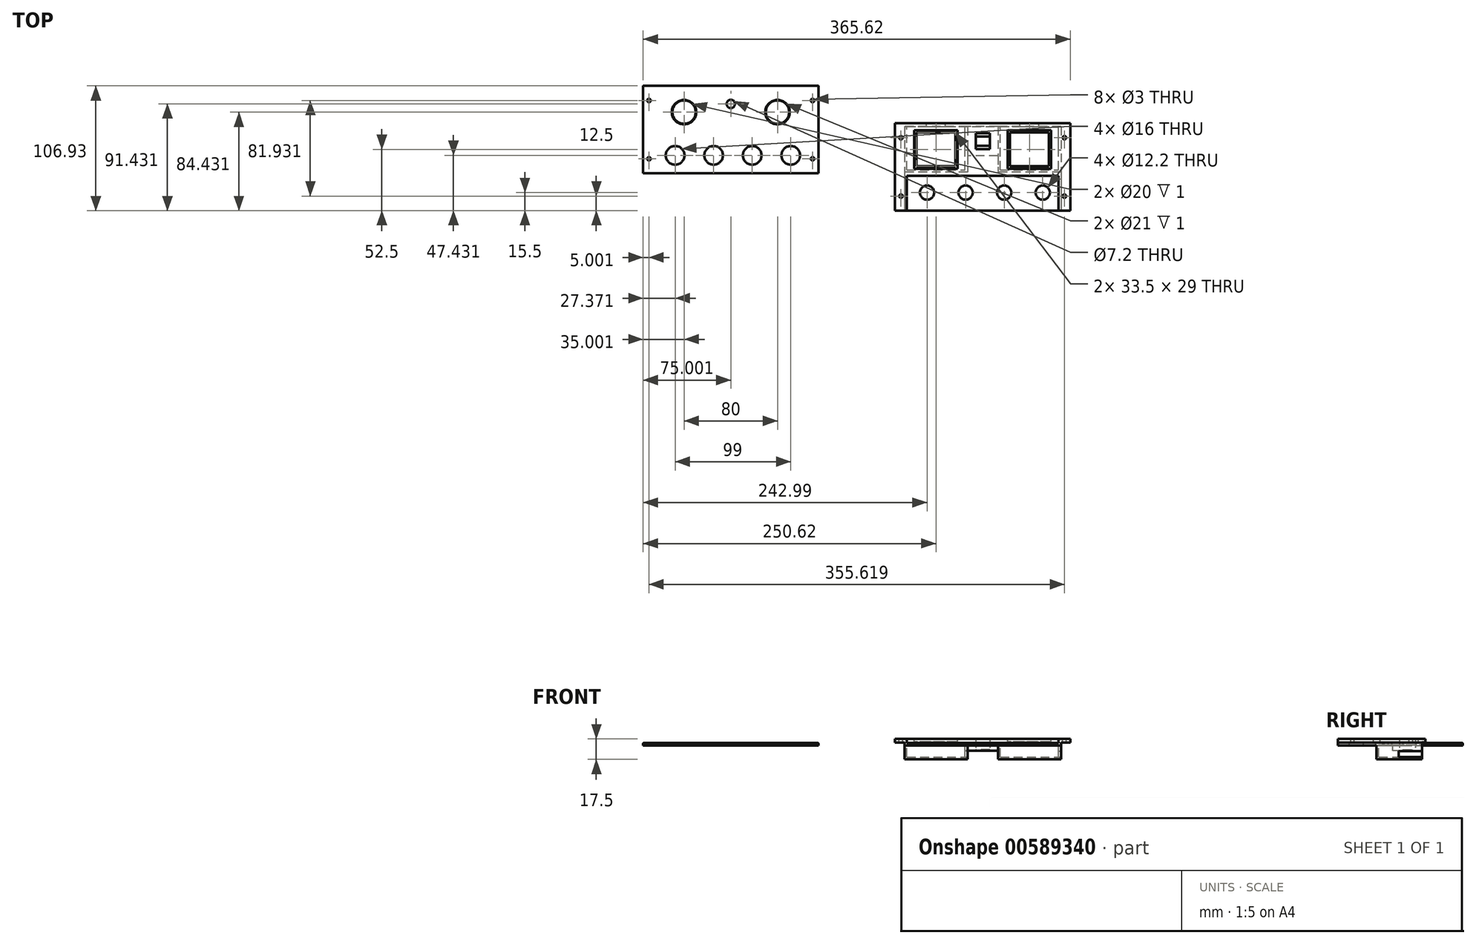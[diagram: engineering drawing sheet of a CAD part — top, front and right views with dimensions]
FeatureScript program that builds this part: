
annotation { "Feature Type Name" : "Feature", "Feature Type Description" : "" }
export const myFeature = defineFeature(function(context is Context, id is Id, definition is map)
    precondition{}
    {
        {
            var Q0;
            Q0=qCreatedBy(makeId("Top.planeOp"),FACE);
            var sketch = newSketch(context, id + "F0", { "sketchPlane" : qUnion([Q0])});
            skLineSegment(sketch, "E0.bottom", {"start": v(75, -37.5) * mm, "end": v(-75, -37.5) * mm});
            skLineSegment(sketch, "E0.top", {"start": v(75, 37.5) * mm, "end": v(-75, 37.5) * mm});
            skLineSegment(sketch, "E0.left", {"start": v(75, -37.5) * mm, "end": v(75, 37.5) * mm});
            skLineSegment(sketch, "E0.right", {"start": v(-75, -37.5) * mm, "end": v(-75, 37.5) * mm});
            skPoint(sketch, "E0.middle", {"position": v(0, 0) * mm});
            skCircle(sketch, "E1", {"center": v(0, 22) * mm, "radius": 5 * mm, "construction": true});
            skCircle(sketch, "E2", {"center": v(-47.63, -22) * mm, "radius": 6.1 * mm});
            skCircle(sketch, "E3.1.0.0", {"center": v(-14.63, -22) * mm, "radius": 6.1 * mm});
            skCircle(sketch, "E3.2.0.0", {"center": v(18.37, -22) * mm, "radius": 6.1 * mm});
            skCircle(sketch, "E3.3.0.0", {"center": v(51.37, -22) * mm, "radius": 6.1 * mm});
            skLineSegment(sketch, "E3.direction1", {"start": v(-47.63, -22) * mm, "end": v(-14.63, -22) * mm, "construction": true});
            skLineSegment(sketch, "E4.bottom", {"start": v(-75, 37.5) * mm, "end": v(-65, 37.5) * mm, "construction": true});
            skLineSegment(sketch, "E4.top", {"start": v(-75, -37.5) * mm, "end": v(-65, -37.5) * mm, "construction": true});
            skLineSegment(sketch, "E4.left", {"start": v(-75, 37.5) * mm, "end": v(-75, -37.5) * mm, "construction": true});
            skLineSegment(sketch, "E4.right", {"start": v(-65, 37.5) * mm, "end": v(-65, -37.5) * mm, "construction": true});
            skLineSegment(sketch, "E5.bottom", {"start": v(75, 37.5) * mm, "end": v(65, 37.5) * mm, "construction": true});
            skLineSegment(sketch, "E5.top", {"start": v(75, -37.5) * mm, "end": v(65, -37.5) * mm, "construction": true});
            skLineSegment(sketch, "E5.left", {"start": v(75, 37.5) * mm, "end": v(75, -37.5) * mm, "construction": true});
            skLineSegment(sketch, "E5.right", {"start": v(65, 37.5) * mm, "end": v(65, -37.5) * mm, "construction": true});
            skPoint(sketch, "E6.middle", {"position": v(-40, 15) * mm});
            skLineSegment(sketch, "E7.bottom", {"start": v(-23.25, 0.5) * mm, "end": v(-56.75, 0.5) * mm});
            skLineSegment(sketch, "E7.top", {"start": v(-23.25, 29.5) * mm, "end": v(-56.75, 29.5) * mm});
            skLineSegment(sketch, "E7.left", {"start": v(-23.25, 0.5) * mm, "end": v(-23.25, 29.5) * mm});
            skLineSegment(sketch, "E7.right", {"start": v(-56.75, 0.5) * mm, "end": v(-56.75, 29.5) * mm});
            skLineSegment(sketch, "E8.bottom", {"start": v(56.75, 0.5) * mm, "end": v(23.25, 0.5) * mm});
            skLineSegment(sketch, "E8.top", {"start": v(56.75, 29.5) * mm, "end": v(23.25, 29.5) * mm});
            skLineSegment(sketch, "E8.left", {"start": v(56.75, 0.5) * mm, "end": v(56.75, 29.5) * mm});
            skLineSegment(sketch, "E8.right", {"start": v(23.25, 0.5) * mm, "end": v(23.25, 29.5) * mm});
            skPoint(sketch, "E8.middle", {"position": v(40, 15) * mm});
            skPoint(sketch, "E9.centerSnap0", {"position": v(-70, 37.5) * mm});
            skCircle(sketch, "E10", {"center": v(-70, 25) * mm, "radius": 1.5 * mm});
            skCircle(sketch, "E11", {"center": v(-70, -25) * mm, "radius": 1.5 * mm});
            skCircle(sketch, "E12", {"center": v(70, 25) * mm, "radius": 1.5 * mm});
            skCircle(sketch, "E13", {"center": v(70, -25) * mm, "radius": 1.5 * mm});
            skLineSegment(sketch, "E14.bottom", {"start": v(6, 15.25) * mm, "end": v(-6, 15.25) * mm});
            skLineSegment(sketch, "E14.top", {"start": v(6, 28.75) * mm, "end": v(-6, 28.75) * mm});
            skLineSegment(sketch, "E14.left", {"start": v(6, 15.25) * mm, "end": v(6, 28.75) * mm});
            skLineSegment(sketch, "E14.right", {"start": v(-6, 15.25) * mm, "end": v(-6, 28.75) * mm});
            skLineSegment(sketch, "E15.bottom", {"start": v(6, 18) * mm, "end": v(-6, 18) * mm});
            skLineSegment(sketch, "E15.top", {"start": v(6, 26) * mm, "end": v(-6, 26) * mm});
            skLineSegment(sketch, "E15.left", {"start": v(6, 18) * mm, "end": v(6, 26) * mm});
            skLineSegment(sketch, "E15.right", {"start": v(-6, 18) * mm, "end": v(-6, 26) * mm});
            skSolve(sketch);
        }
        {
            var Q0;
            Q0=makeQuery(id+"F0.imprint","IMPRINT",FACE,{"disambiguationData":[TD([[makeQuery(id+"F0.imprint","IMPRINT",EDGE,{"derivedFrom":sQuery(id+"F0.wireOp",EDGE,"E0.bottom")}),-1.0]])]});
            var Q1;
            Q1=makeQuery(id+"F0.imprint","IMPRINT",FACE,{"disambiguationData":[TD([[makeQuery(id+"F0.imprint","IMPRINT",EDGE,{"derivedFrom":sQuery(id+"F0.wireOp",EDGE,"drD5jItb-HEpr-sxaA-TqkW-DfUxLCmm6Exs")}),-1.0]])]});
            var Q2;
            Q2=makeQuery(id+"F0.imprint","IMPRINT",FACE,{"disambiguationData":[TD([[makeQuery(id+"F0.imprint","IMPRINT",EDGE,{"derivedFrom":sQuery(id+"F0.wireOp",EDGE,"E15.bottom")}),-1.0]])]});
            extrude(context, id + "F1", {"entities" : qUnion([Q0, Q1, Q2]), "depth" : 2 * mm});
        }
        {
            var Q0;
            Q0=makeQuery(id+"F1.opExtrude","CAP_FACE",FACE,{"disambiguationData":[OSD([sQuery(id+"F0.wireOp",EDGE,"E0.bottom"),sQuery(id+"F0.wireOp",EDGE,"E0.top"),sQuery(id+"F0.wireOp",EDGE,"E0.left"),sQuery(id+"F0.wireOp",EDGE,"E0.right"),sQuery(id+"F0.wireOp",EDGE,"drD5jItb-HEpr-sxaA-TqkW-DfUxLCmm6Exs"),sQuery(id+"F0.wireOp",EDGE,"oSn99fef-1uPw-k3Do-L9e6-x1k65rtnndGm"),sQuery(id+"F0.wireOp",EDGE,"E1"),sQuery(id+"F0.wireOp",EDGE,"E2"),sQuery(id+"F0.wireOp",EDGE,"E3.1.0.0"),sQuery(id+"F0.wireOp",EDGE,"E3.2.0.0"),sQuery(id+"F0.wireOp",EDGE,"E3.3.0.0")])],"isStart":false});
            var sketch = newSketch(context, id + "F2", { "sketchPlane" : qUnion([Q0])});
            skLineSegment(sketch, "E16.bottom", {"start": v(-75, 37.5) * mm, "end": v(-65, 37.5) * mm});
            skLineSegment(sketch, "E16.top", {"start": v(-75, -37.5) * mm, "end": v(-65, -37.5) * mm});
            skLineSegment(sketch, "E16.left", {"start": v(-75, 37.5) * mm, "end": v(-75, -37.5) * mm});
            skLineSegment(sketch, "E16.right", {"start": v(-65, 37.5) * mm, "end": v(-65, -37.5) * mm});
            skLineSegment(sketch, "E17.bottom", {"start": v(75, -37.5) * mm, "end": v(65, -37.5) * mm});
            skLineSegment(sketch, "E17.top", {"start": v(75, 37.5) * mm, "end": v(65, 37.5) * mm});
            skLineSegment(sketch, "E17.left", {"start": v(75, -37.5) * mm, "end": v(75, 37.5) * mm});
            skLineSegment(sketch, "E17.right", {"start": v(65, -37.5) * mm, "end": v(65, 37.5) * mm});
            skSolve(sketch);
        }
        {
            var Q0;
            Q0=qSketchRegion(id+"F2",true);
            extrude(context, id + "F3", {"entities" : qUnion([Q0]), "operationType" : NewBodyOperationType.ADD, "depth" : 3.5 * mm});
        }
        {
            var Q0;
            Q0=makeQuery(id+"F3.boolean.opBoolean","MERGE",FACE,{"derivedFrom":[makeQuery(id+"F1.opExtrude","SWEPT_FACE",FACE,{"disambiguationData":[OSD([sQuery(id+"F0.wireOp",EDGE,"E0.bottom")])]}),makeQuery(id+"F3.opExtrude","SWEPT_FACE",FACE,{"disambiguationData":[OSD([sQuery(id+"F2.wireOp",EDGE,"E16.top")])]}),makeQuery(id+"F3.opExtrude","SWEPT_FACE",FACE,{"disambiguationData":[OSD([sQuery(id+"F2.wireOp",EDGE,"E17.bottom")])]})]});
            var sketch = newSketch(context, id + "F4", { "sketchPlane" : qUnion([Q0])});
            skLineSegment(sketch, "E18.bottom", {"start": v(-75, 0) * mm, "end": v(-67, 0) * mm});
            skLineSegment(sketch, "E18.top", {"start": v(-75, 2.5) * mm, "end": v(-67, 2.5) * mm});
            skLineSegment(sketch, "E18.left", {"start": v(-75, 0) * mm, "end": v(-75, 2.5) * mm});
            skLineSegment(sketch, "E18.right", {"start": v(-67, 0) * mm, "end": v(-67, 2.5) * mm});
            skLineSegment(sketch, "E19.bottom", {"start": v(75, 0) * mm, "end": v(67, 0) * mm});
            skLineSegment(sketch, "E19.top", {"start": v(75, 2.5) * mm, "end": v(67, 2.5) * mm});
            skLineSegment(sketch, "E19.left", {"start": v(75, 0) * mm, "end": v(75, 2.5) * mm});
            skLineSegment(sketch, "E19.right", {"start": v(67, 0) * mm, "end": v(67, 2.5) * mm});
            skSolve(sketch);
        }
        {
            var Q0;
            Q0=qSketchRegion(id+"F4",true);
            extrude(context, id + "F5", {"entities" : qUnion([Q0]), "operationType" : NewBodyOperationType.REMOVE, "oppositeDirection" : true, "depth" : 80 * mm});
        }
        {
            var Q0;
            Q0=makeQuery(id+"F1.opExtrude","CAP_FACE",FACE,{"disambiguationData":[OSD([sQuery(id+"F0.wireOp",EDGE,"E0.bottom"),sQuery(id+"F0.wireOp",EDGE,"E0.top"),sQuery(id+"F0.wireOp",EDGE,"E0.left"),sQuery(id+"F0.wireOp",EDGE,"E0.right"),sQuery(id+"F0.wireOp",EDGE,"drD5jItb-HEpr-sxaA-TqkW-DfUxLCmm6Exs"),sQuery(id+"F0.wireOp",EDGE,"oSn99fef-1uPw-k3Do-L9e6-x1k65rtnndGm"),sQuery(id+"F0.wireOp",EDGE,"E1"),sQuery(id+"F0.wireOp",EDGE,"E2"),sQuery(id+"F0.wireOp",EDGE,"E3.1.0.0"),sQuery(id+"F0.wireOp",EDGE,"E3.2.0.0"),sQuery(id+"F0.wireOp",EDGE,"E3.3.0.0")])],"isStart":false});
            var sketch = newSketch(context, id + "F6", { "sketchPlane" : qUnion([Q0])});
            skLineSegment(sketch, "E20.bottom", {"start": v(-65, 37.5) * mm, "end": v(65, 37.5) * mm});
            skLineSegment(sketch, "E20.top", {"start": v(-65, -7.5) * mm, "end": v(65, -7.5) * mm});
            skLineSegment(sketch, "E20.left", {"start": v(-65, 37.5) * mm, "end": v(-65, -7.5) * mm});
            skLineSegment(sketch, "E20.right", {"start": v(65, 37.5) * mm, "end": v(65, -7.5) * mm});
            skCircle(sketch, "E21", {"center": v(0, 22) * mm, "radius": 5 * mm, "construction": true});
            skLineSegment(sketch, "E22.bottom", {"start": v(-23.25, 0.5) * mm, "end": v(-56.75, 0.5) * mm});
            skLineSegment(sketch, "E22.top", {"start": v(-23.25, 29.5) * mm, "end": v(-56.75, 29.5) * mm});
            skLineSegment(sketch, "E22.left", {"start": v(-23.25, 0.5) * mm, "end": v(-23.25, 29.5) * mm});
            skLineSegment(sketch, "E22.right", {"start": v(-56.75, 0.5) * mm, "end": v(-56.75, 29.5) * mm});
            skPoint(sketch, "E22.middle", {"position": v(-40, 15) * mm});
            skLineSegment(sketch, "E23.bottom", {"start": v(56.75, 0.5) * mm, "end": v(23.25, 0.5) * mm});
            skLineSegment(sketch, "E23.top", {"start": v(56.75, 29.5) * mm, "end": v(23.25, 29.5) * mm});
            skLineSegment(sketch, "E23.left", {"start": v(56.75, 0.5) * mm, "end": v(56.75, 29.5) * mm});
            skLineSegment(sketch, "E23.right", {"start": v(23.25, 0.5) * mm, "end": v(23.25, 29.5) * mm});
            skPoint(sketch, "E23.middle", {"position": v(40, 15) * mm});
            skLineSegment(sketch, "E24.bottom", {"start": v(6, 15.25) * mm, "end": v(-6, 15.25) * mm});
            skLineSegment(sketch, "E24.top", {"start": v(6, 28.75) * mm, "end": v(-6, 28.75) * mm});
            skLineSegment(sketch, "E24.left", {"start": v(6, 15.25) * mm, "end": v(6, 28.75) * mm});
            skLineSegment(sketch, "E24.right", {"start": v(-6, 15.25) * mm, "end": v(-6, 28.75) * mm});
            skSolve(sketch);
        }
        {
            var Q0;
            Q0=qSketchRegion(id+"F6",true);
            extrude(context, id + "F7", {"entities" : qUnion([Q0]), "operationType" : NewBodyOperationType.ADD, "depth" : 3.5 * mm});
        }
        {
            var Q0;
            Q0=makeQuery(id+"F7.boolean.opBoolean","MERGE",FACE,{"derivedFrom":[makeQuery(id+"F3.opExtrude","CAP_FACE",FACE,{"disambiguationData":[OSD([sQuery(id+"F2.wireOp",EDGE,"E16.bottom"),sQuery(id+"F2.wireOp",EDGE,"E16.top"),sQuery(id+"F2.wireOp",EDGE,"E16.left"),sQuery(id+"F2.wireOp",EDGE,"E16.right")])],"isStart":false}),makeQuery(id+"F3.opExtrude","CAP_FACE",FACE,{"disambiguationData":[OSD([sQuery(id+"F2.wireOp",EDGE,"E17.bottom"),sQuery(id+"F2.wireOp",EDGE,"E17.top"),sQuery(id+"F2.wireOp",EDGE,"E17.left"),sQuery(id+"F2.wireOp",EDGE,"E17.right")])],"isStart":false}),makeQuery(id+"F7.opExtrude","CAP_FACE",FACE,{"disambiguationData":[OSD([sQuery(id+"F6.wireOp",EDGE,"E20.bottom"),sQuery(id+"F6.wireOp",EDGE,"E20.top"),sQuery(id+"F6.wireOp",EDGE,"E20.left"),sQuery(id+"F6.wireOp",EDGE,"E20.right"),sQuery(id+"F6.wireOp",EDGE,"H2Zb9yD0-p2Z7-Kh5e-a6hj-aLUdcpXocAIw"),sQuery(id+"F6.wireOp",EDGE,"7ZJ2aJG6-LJXW-fwXF-v4kC-qdLRGwjfnqPK"),sQuery(id+"F6.wireOp",EDGE,"E21")])],"isStart":false})]});
            var sketch = newSketch(context, id + "F8", { "sketchPlane" : qUnion([Q0])});
            skLineSegment(sketch, "E25.bottom", {"start": v(-21.4, -1.5) * mm, "end": v(-58.6, -1.5) * mm});
            skLineSegment(sketch, "E25.top", {"start": v(-21.4, 31.5) * mm, "end": v(-58.6, 31.5) * mm});
            skLineSegment(sketch, "E25.left", {"start": v(-21.4, -1.5) * mm, "end": v(-21.4, 31.5) * mm});
            skLineSegment(sketch, "E25.right", {"start": v(-58.6, -1.5) * mm, "end": v(-58.6, 31.5) * mm});
            skPoint(sketch, "E25.middle", {"position": v(-40, 15) * mm});
            skLineSegment(sketch, "E26.bottom", {"start": v(58.6, -1.5) * mm, "end": v(21.4, -1.5) * mm});
            skLineSegment(sketch, "E26.top", {"start": v(58.6, 31.5) * mm, "end": v(21.4, 31.5) * mm});
            skLineSegment(sketch, "E26.left", {"start": v(58.6, -1.5) * mm, "end": v(58.6, 31.5) * mm});
            skLineSegment(sketch, "E26.right", {"start": v(21.4, -1.5) * mm, "end": v(21.4, 31.5) * mm});
            skPoint(sketch, "E26.middle", {"position": v(40, 15) * mm});
            skLineSegment(sketch, "E27.bottom", {"start": v(-32, 31.5) * mm, "end": v(-48, 31.5) * mm});
            skLineSegment(sketch, "E27.top", {"start": v(-32, 46.5) * mm, "end": v(-48, 46.5) * mm});
            skLineSegment(sketch, "E27.left", {"start": v(-32, 31.5) * mm, "end": v(-32, 46.5) * mm});
            skLineSegment(sketch, "E27.right", {"start": v(-48, 31.5) * mm, "end": v(-48, 46.5) * mm});
            skPoint(sketch, "E27.middle", {"position": v(-40, 39) * mm});
            skPoint(sketch, "E27.middle.positionSnap0", {"position": v(-40, 31.5) * mm});
            skPoint(sketch, "E27.centerSnap0", {"position": v(-40, 31.5) * mm});
            skLineSegment(sketch, "E28.bottom", {"start": v(48, 31.5) * mm, "end": v(32, 31.5) * mm});
            skLineSegment(sketch, "E28.top", {"start": v(48, 46.5) * mm, "end": v(32, 46.5) * mm});
            skLineSegment(sketch, "E28.left", {"start": v(48, 31.5) * mm, "end": v(48, 46.5) * mm});
            skLineSegment(sketch, "E28.right", {"start": v(32, 31.5) * mm, "end": v(32, 46.5) * mm});
            skPoint(sketch, "E28.middle", {"position": v(40, 39) * mm});
            skPoint(sketch, "E28.middle.positionSnap0", {"position": v(40, 31.5) * mm});
            skPoint(sketch, "E28.centerSnap0", {"position": v(40, 31.5) * mm});
            skSolve(sketch);
        }
        {
            var Q0;
            Q0=makeQuery(id+"F8.imprint","IMPRINT",FACE,{"disambiguationData":[TD([[makeQuery(id+"F8.imprint","IMPRINT",EDGE,{"derivedFrom":sQuery(id+"F8.wireOp",EDGE,"E25.bottom")}),-1.0]])]});
            var Q1;
            Q1=makeQuery(id+"F8.imprint","IMPRINT",FACE,{"disambiguationData":[TD([[makeQuery(id+"F8.imprint","IMPRINT",EDGE,{"derivedFrom":sQuery(id+"F8.wireOp",EDGE,"E26.bottom")}),-1.0]])]});
            var Q2;
            {var subQ0=sQuery(id+"F8.wireOp",EDGE,"E27.top");Q2=makeQuery(id+"F8.imprint","IMPRINT",FACE,{"disambiguationData":[TD([[makeQuery(id+"F8.imprint","IMPRINT",EDGE,{"derivedFrom":subQ0}),1.0]])]});}
            var Q3;
            {var subQ0=sQuery(id+"F8.wireOp",EDGE,"E28.top");Q3=makeQuery(id+"F8.imprint","IMPRINT",FACE,{"disambiguationData":[TD([[makeQuery(id+"F8.imprint","IMPRINT",EDGE,{"derivedFrom":subQ0}),1.0]])]});}
            var Q4;
            {var subQ0=sQuery(id+"F8.wireOp",EDGE,"E27.bottom");Q4=makeQuery(id+"F8.imprint","IMPRINT",FACE,{"disambiguationData":[TD([[makeQuery(id+"F8.imprint","IMPRINT",EDGE,{"derivedFrom":subQ0}),-1.0]])]});}
            var Q5;
            {var subQ0=sQuery(id+"F8.wireOp",EDGE,"E28.bottom");Q5=makeQuery(id+"F8.imprint","IMPRINT",FACE,{"disambiguationData":[TD([[makeQuery(id+"F8.imprint","IMPRINT",EDGE,{"derivedFrom":subQ0}),-1.0]])]});}
            extrude(context, id + "F9", {"entities" : qUnion([Q0, Q1, Q2, Q3, Q4, Q5]), "operationType" : NewBodyOperationType.REMOVE, "oppositeDirection" : true, "depth" : 2.5 * mm});
        }
        {
            var Q0;
            Q0=qCreatedBy(makeId("Top.planeOp"),FACE);
            var sketch = newSketch(context, id + "F10", { "sketchPlane" : qUnion([Q0])});
            skLineSegment(sketch, "E29.bottom", {"start": v(-140.62, -5.57) * mm, "end": v(-290.62, -5.57) * mm});
            skLineSegment(sketch, "E29.top", {"start": v(-140.62, 69.43) * mm, "end": v(-290.62, 69.43) * mm});
            skLineSegment(sketch, "E29.left", {"start": v(-140.62, -5.57) * mm, "end": v(-140.62, 69.43) * mm});
            skLineSegment(sketch, "E29.right", {"start": v(-290.62, -5.57) * mm, "end": v(-290.62, 69.43) * mm});
            skPoint(sketch, "E29.middle", {"position": v(-215.62, 31.93) * mm});
            skCircle(sketch, "E30", {"center": v(-215.62, 53.93) * mm, "radius": 3.6 * mm});
            skCircle(sketch, "E31", {"center": v(-263.25, 9.93) * mm, "radius": 8 * mm});
            skCircle(sketch, "E32.1.0.0", {"center": v(-230.25, 9.93) * mm, "radius": 8 * mm});
            skCircle(sketch, "E32.2.0.0", {"center": v(-197.25, 9.93) * mm, "radius": 8 * mm});
            skCircle(sketch, "E32.3.0.0", {"center": v(-164.25, 9.93) * mm, "radius": 8 * mm});
            skLineSegment(sketch, "E32.direction1", {"start": v(-263.25, 9.93) * mm, "end": v(-230.25, 9.93) * mm, "construction": true});
            skLineSegment(sketch, "E33.bottom", {"start": v(-290.62, 69.43) * mm, "end": v(-280.62, 69.43) * mm, "construction": true});
            skLineSegment(sketch, "E33.top", {"start": v(-290.62, -5.57) * mm, "end": v(-280.62, -5.57) * mm, "construction": true});
            skLineSegment(sketch, "E33.left", {"start": v(-290.62, 69.43) * mm, "end": v(-290.62, -5.57) * mm, "construction": true});
            skLineSegment(sketch, "E33.right", {"start": v(-280.62, 69.43) * mm, "end": v(-280.62, -5.57) * mm, "construction": true});
            skLineSegment(sketch, "E34.bottom", {"start": v(-140.62, 69.43) * mm, "end": v(-150.62, 69.43) * mm, "construction": true});
            skLineSegment(sketch, "E34.top", {"start": v(-140.62, -5.57) * mm, "end": v(-150.62, -5.57) * mm, "construction": true});
            skLineSegment(sketch, "E34.left", {"start": v(-140.62, 69.43) * mm, "end": v(-140.62, -5.57) * mm, "construction": true});
            skLineSegment(sketch, "E34.right", {"start": v(-150.62, 69.43) * mm, "end": v(-150.62, -5.57) * mm, "construction": true});
            skPoint(sketch, "E35.middle", {"position": v(-255.62, 46.93) * mm});
            skPoint(sketch, "E36.middle", {"position": v(-175.62, 46.93) * mm});
            skCircle(sketch, "E37", {"center": v(-255.62, 46.93) * mm, "radius": 10 * mm});
            skCircle(sketch, "E38", {"center": v(-175.62, 46.93) * mm, "radius": 10 * mm});
            skLineSegment(sketch, "E39.bottom", {"start": v(-236.87, 30.43) * mm, "end": v(-274.37, 30.43) * mm, "construction": true});
            skLineSegment(sketch, "E39.top", {"start": v(-236.87, 63.43) * mm, "end": v(-274.37, 63.43) * mm, "construction": true});
            skLineSegment(sketch, "E39.left", {"start": v(-236.87, 30.43) * mm, "end": v(-236.87, 63.43) * mm, "construction": true});
            skLineSegment(sketch, "E39.right", {"start": v(-274.37, 30.43) * mm, "end": v(-274.37, 63.43) * mm, "construction": true});
            skLineSegment(sketch, "E40.bottom", {"start": v(-156.87, 30.43) * mm, "end": v(-194.37, 30.43) * mm, "construction": true});
            skLineSegment(sketch, "E40.top", {"start": v(-156.87, 63.43) * mm, "end": v(-194.37, 63.43) * mm, "construction": true});
            skLineSegment(sketch, "E40.left", {"start": v(-156.87, 30.43) * mm, "end": v(-156.87, 63.43) * mm, "construction": true});
            skLineSegment(sketch, "E40.right", {"start": v(-194.37, 30.43) * mm, "end": v(-194.37, 63.43) * mm, "construction": true});
            skCircle(sketch, "E41", {"center": v(-285.62, 56.93) * mm, "radius": 1.5 * mm});
            skCircle(sketch, "E42", {"center": v(-285.62, 6.93) * mm, "radius": 1.5 * mm});
            skCircle(sketch, "E43", {"center": v(-145.62, 56.93) * mm, "radius": 1.5 * mm});
            skCircle(sketch, "E44", {"center": v(-145.62, 6.93) * mm, "radius": 1.5 * mm});
            skSolve(sketch);
        }
        {
            var Q0;
            Q0=makeQuery(id+"F10.imprint","IMPRINT",FACE,{"disambiguationData":[TD([[makeQuery(id+"F10.imprint","IMPRINT",EDGE,{"derivedFrom":sQuery(id+"F10.wireOp",EDGE,"E29.bottom")}),-1.0]])]});
            extrude(context, id + "F11", {"entities" : qUnion([Q0]), "depth" : 2 * mm});
        }
        {
            var Q0;
            Q0=makeQuery(id+"F11.opExtrude","CAP_FACE",FACE,{"disambiguationData":[OSD([sQuery(id+"F10.wireOp",EDGE,"E29.bottom"),sQuery(id+"F10.wireOp",EDGE,"E29.top"),sQuery(id+"F10.wireOp",EDGE,"E29.left"),sQuery(id+"F10.wireOp",EDGE,"E29.right"),sQuery(id+"F10.wireOp",EDGE,"E30"),sQuery(id+"F10.wireOp",EDGE,"E31"),sQuery(id+"F10.wireOp",EDGE,"E32.1.0.0"),sQuery(id+"F10.wireOp",EDGE,"E32.2.0.0"),sQuery(id+"F10.wireOp",EDGE,"E32.3.0.0"),sQuery(id+"F10.wireOp",EDGE,"E37"),sQuery(id+"F10.wireOp",EDGE,"E38")])],"isStart":false});
            var sketch = newSketch(context, id + "F12", { "sketchPlane" : qUnion([Q0])});
            skLineSegment(sketch, "E45.bottom", {"start": v(-239.12, 65.68) * mm, "end": v(-272.12, 65.68) * mm, "construction": true});
            skLineSegment(sketch, "E45.top", {"start": v(-239.12, 28.18) * mm, "end": v(-272.12, 28.18) * mm, "construction": true});
            skLineSegment(sketch, "E45.left", {"start": v(-239.12, 65.68) * mm, "end": v(-239.12, 28.18) * mm, "construction": true});
            skLineSegment(sketch, "E45.right", {"start": v(-272.12, 65.68) * mm, "end": v(-272.12, 28.18) * mm, "construction": true});
            skPoint(sketch, "E45.middle", {"position": v(-255.62, 46.93) * mm});
            skLineSegment(sketch, "E46.bottom", {"start": v(-159.12, 65.68) * mm, "end": v(-192.12, 65.68) * mm, "construction": true});
            skLineSegment(sketch, "E46.top", {"start": v(-159.12, 28.18) * mm, "end": v(-192.12, 28.18) * mm, "construction": true});
            skLineSegment(sketch, "E46.left", {"start": v(-159.12, 65.68) * mm, "end": v(-159.12, 28.18) * mm, "construction": true});
            skLineSegment(sketch, "E46.right", {"start": v(-192.12, 65.68) * mm, "end": v(-192.12, 28.18) * mm, "construction": true});
            skPoint(sketch, "E46.middle", {"position": v(-175.62, 46.93) * mm});
            skCircle(sketch, "E47", {"center": v(-255.62, 46.93) * mm, "radius": 10.5 * mm});
            skCircle(sketch, "E48", {"center": v(-175.62, 46.93) * mm, "radius": 10.5 * mm});
            skSolve(sketch);
        }
        {
            var Q0;
            Q0=qSketchRegion(id+"F12",true);
            extrude(context, id + "F13", {"entities" : qUnion([Q0]), "operationType" : NewBodyOperationType.REMOVE, "oppositeDirection" : true, "depth" : 1 * mm});
        }
        {
            var Q0;
            Q0=makeQuery(id+"F0.imprint","IMPRINT",FACE,{"disambiguationData":[TD([[makeQuery(id+"F0.imprint","IMPRINT",EDGE,{"derivedFrom":sQuery(id+"F0.wireOp",EDGE,"E0.bottom")}),-1.0]])]});
            var sketch = newSketch(context, id + "F14", { "sketchPlane" : qUnion([Q0])});
            skPoint(sketch, "E49.0", {"position": v(0, 22) * mm});
            skLineSegment(sketch, "E50.bottom", {"start": v(13, 34.5) * mm, "end": v(-13, 34.5) * mm});
            skLineSegment(sketch, "E50.top", {"start": v(13, 9.5) * mm, "end": v(-13, 9.5) * mm});
            skLineSegment(sketch, "E50.left", {"start": v(13, 34.5) * mm, "end": v(13, 9.5) * mm});
            skLineSegment(sketch, "E50.right", {"start": v(-13, 34.5) * mm, "end": v(-13, 9.5) * mm});
            skPoint(sketch, "E51.0", {"position": v(6, 26) * mm});
            skLineSegment(sketch, "E52.bottom", {"start": v(6, 26) * mm, "end": v(-6, 26) * mm});
            skLineSegment(sketch, "E52.top", {"start": v(6, 18) * mm, "end": v(-6, 18) * mm});
            skLineSegment(sketch, "E52.left", {"start": v(6, 26) * mm, "end": v(6, 18) * mm});
            skLineSegment(sketch, "E52.right", {"start": v(-6, 26) * mm, "end": v(-6, 18) * mm});
            skSolve(sketch);
        }
        {
            var Q0;
            Q0=makeQuery(id+"F14.imprint","IMPRINT",FACE,{"disambiguationData":[TD([[makeQuery(id+"F14.imprint","IMPRINT",EDGE,{"derivedFrom":sQuery(id+"F14.wireOp",EDGE,"E50.bottom")}),1.0]])]});
            var Q1;
            Q1=makeQuery(id+"F0.imprint","IMPRINT",FACE,{"disambiguationData":[TD([[makeQuery(id+"F0.imprint","IMPRINT",EDGE,{"derivedFrom":sQuery(id+"F0.wireOp",EDGE,"E15.bottom")}),-1.0]])]});
            extrude(context, id + "F15", {"entities" : qUnion([Q0, Q1]), "operationType" : NewBodyOperationType.ADD, "oppositeDirection" : true, "depth" : 4.5 * mm});
        }
        {
            var Q0;
            Q0=makeQuery(id+"F7.boolean.opBoolean","MERGE",FACE,{"derivedFrom":[makeQuery(id+"F3.opExtrude","CAP_FACE",FACE,{"disambiguationData":[OSD([sQuery(id+"F2.wireOp",EDGE,"E16.bottom"),sQuery(id+"F2.wireOp",EDGE,"E16.top"),sQuery(id+"F2.wireOp",EDGE,"E16.left"),sQuery(id+"F2.wireOp",EDGE,"E16.right")])],"isStart":false}),makeQuery(id+"F3.opExtrude","CAP_FACE",FACE,{"disambiguationData":[OSD([sQuery(id+"F2.wireOp",EDGE,"E17.bottom"),sQuery(id+"F2.wireOp",EDGE,"E17.top"),sQuery(id+"F2.wireOp",EDGE,"E17.left"),sQuery(id+"F2.wireOp",EDGE,"E17.right")])],"isStart":false}),makeQuery(id+"F7.opExtrude","CAP_FACE",FACE,{"disambiguationData":[OSD([sQuery(id+"F6.wireOp",EDGE,"E20.bottom"),sQuery(id+"F6.wireOp",EDGE,"E20.top"),sQuery(id+"F6.wireOp",EDGE,"E20.left"),sQuery(id+"F6.wireOp",EDGE,"E20.right"),sQuery(id+"F6.wireOp",EDGE,"E22.bottom"),sQuery(id+"F6.wireOp",EDGE,"E22.top"),sQuery(id+"F6.wireOp",EDGE,"E22.left"),sQuery(id+"F6.wireOp",EDGE,"E22.right"),sQuery(id+"F6.wireOp",EDGE,"E23.bottom"),sQuery(id+"F6.wireOp",EDGE,"E23.top"),sQuery(id+"F6.wireOp",EDGE,"E23.left"),sQuery(id+"F6.wireOp",EDGE,"E23.right"),sQuery(id+"F6.wireOp",EDGE,"E24.bottom"),sQuery(id+"F6.wireOp",EDGE,"E24.top"),sQuery(id+"F6.wireOp",EDGE,"E24.left"),sQuery(id+"F6.wireOp",EDGE,"E24.right")])],"isStart":false})]});
            var sketch = newSketch(context, id + "F16", { "sketchPlane" : qUnion([Q0])});
            skPoint(sketch, "E53.0", {"position": v(0, 22) * mm});
            skLineSegment(sketch, "E54.bottom", {"start": v(6, 15.25) * mm, "end": v(-6, 15.25) * mm});
            skLineSegment(sketch, "E54.top", {"start": v(6, 28.75) * mm, "end": v(-6, 28.75) * mm});
            skLineSegment(sketch, "E54.left", {"start": v(6, 15.25) * mm, "end": v(6, 28.75) * mm});
            skLineSegment(sketch, "E54.right", {"start": v(-6, 15.25) * mm, "end": v(-6, 28.75) * mm});
            skSolve(sketch);
        }
        {
            var Q0;
            Q0=qSketchRegion(id+"F16",true);
            extrude(context, id + "F17", {"entities" : qUnion([Q0]), "operationType" : NewBodyOperationType.REMOVE, "oppositeDirection" : true, "depth" : 9 * mm});
        }
        {
            var Q0;
            Q0=makeQuery(id+"F0.imprint","IMPRINT",FACE,{"disambiguationData":[TD([[makeQuery(id+"F0.imprint","IMPRINT",EDGE,{"derivedFrom":sQuery(id+"F0.wireOp",EDGE,"E0.bottom")}),-1.0]])]});
            var sketch = newSketch(context, id + "F18", { "sketchPlane" : qUnion([Q0])});
            skPoint(sketch, "E55.0", {"position": v(-67, 37.5) * mm});
            skPoint(sketch, "E55.1", {"position": v(67, 37.5) * mm});
            skLineSegment(sketch, "E56.bottom", {"start": v(-67, 37.5) * mm, "end": v(67, 37.5) * mm});
            skLineSegment(sketch, "E56.top", {"start": v(-67, 34.5) * mm, "end": v(67, 34.5) * mm});
            skLineSegment(sketch, "E56.left", {"start": v(-67, 37.5) * mm, "end": v(-67, 34.5) * mm});
            skLineSegment(sketch, "E56.right", {"start": v(67, 37.5) * mm, "end": v(67, 34.5) * mm});
            skSolve(sketch);
        }
        {
            var Q0;
            Q0=makeQuery(id+"F18.imprint","IMPRINT",FACE,{"disambiguationData":[TD([[makeQuery(id+"F18.imprint","IMPRINT",EDGE,{"derivedFrom":sQuery(id+"F18.wireOp",EDGE,"E56.bottom")}),1.0]])]});
            extrude(context, id + "F19", {"entities" : qUnion([Q0]), "operationType" : NewBodyOperationType.REMOVE, "depth" : 2.5 * mm});
        }
        {
            var Q0;
            Q0=makeQuery(id+"F0.imprint","IMPRINT",FACE,{"disambiguationData":[TD([[makeQuery(id+"F0.imprint","IMPRINT",EDGE,{"derivedFrom":sQuery(id+"F0.wireOp",EDGE,"E0.bottom")}),-1.0]])]});
            var sketch = newSketch(context, id + "F20", { "sketchPlane" : qUnion([Q0])});
            skPoint(sketch, "E57.0", {"position": v(-40, 15) * mm});
            skPoint(sketch, "E57.1", {"position": v(40, 15) * mm});
            skLineSegment(sketch, "E58.bottom", {"start": v(-13, 34.5) * mm, "end": v(-67, 34.5) * mm});
            skLineSegment(sketch, "E58.top", {"start": v(-13, -4.5) * mm, "end": v(-67, -4.5) * mm});
            skLineSegment(sketch, "E58.left", {"start": v(-13, 34.5) * mm, "end": v(-13, -4.5) * mm});
            skLineSegment(sketch, "E58.right", {"start": v(-67, 34.5) * mm, "end": v(-67, -4.5) * mm});
            skLineSegment(sketch, "E59.bottom", {"start": v(67, 34.5) * mm, "end": v(13, 34.5) * mm});
            skLineSegment(sketch, "E59.top", {"start": v(67, -4.5) * mm, "end": v(13, -4.5) * mm});
            skLineSegment(sketch, "E59.left", {"start": v(67, 34.5) * mm, "end": v(67, -4.5) * mm});
            skLineSegment(sketch, "E59.right", {"start": v(13, 34.5) * mm, "end": v(13, -4.5) * mm});
            skSolve(sketch);
        }
        {
            var Q0;
            Q0=makeQuery(id+"F20.imprint","IMPRINT",FACE,{"disambiguationData":[TD([[makeQuery(id+"F20.imprint","IMPRINT",EDGE,{"derivedFrom":sQuery(id+"F20.wireOp",EDGE,"E59.bottom")}),1.0]])]});
            var Q1;
            Q1=makeQuery(id+"F20.imprint","IMPRINT",FACE,{"disambiguationData":[TD([[makeQuery(id+"F20.imprint","IMPRINT",EDGE,{"derivedFrom":sQuery(id+"F20.wireOp",EDGE,"E58.bottom")}),1.0]])]});
            var Q2;
            Q2=makeQuery(id+"F20.imprint","IMPRINT",FACE,{"disambiguationData":[TD([[makeQuery(id+"F20.imprint","IMPRINT",EDGE,{"derivedFrom":makeQuery(id+"F0.imprint","IMPRINT",EDGE,{"derivedFrom":sQuery(id+"F0.wireOp",EDGE,"E8.bottom")})}),-1.0]])]});
            var Q3;
            Q3=makeQuery(id+"F20.imprint","IMPRINT",FACE,{"disambiguationData":[TD([[makeQuery(id+"F20.imprint","IMPRINT",EDGE,{"derivedFrom":makeQuery(id+"F0.imprint","IMPRINT",EDGE,{"derivedFrom":sQuery(id+"F0.wireOp",EDGE,"E7.bottom")})}),-1.0]])]});
            extrude(context, id + "F21", {"entities" : qUnion([Q0, Q1, Q2, Q3]), "operationType" : NewBodyOperationType.ADD, "oppositeDirection" : true, "depth" : 12 * mm});
        }
        {
            var Q0;
            Q0=makeQuery(id+"F21.boolean.opBoolean","MERGE",FACE,{"derivedFrom":[makeQuery(id+"F19.boolean.opBoolean","MERGE",FACE,{"derivedFrom":[makeQuery(id+"F15.opExtrude","SWEPT_FACE",FACE,{"disambiguationData":[OSD([sQuery(id+"F14.wireOp",EDGE,"E50.bottom")])]}),makeQuery(id+"F19.opExtrude","SWEPT_FACE",FACE,{"disambiguationData":[OSD([sQuery(id+"F18.wireOp",EDGE,"E56.top")])]})]}),makeQuery(id+"F21.opExtrude","SWEPT_FACE",FACE,{"disambiguationData":[OSD([sQuery(id+"F20.wireOp",EDGE,"E58.bottom")])]}),makeQuery(id+"F21.opExtrude","SWEPT_FACE",FACE,{"disambiguationData":[OSD([sQuery(id+"F20.wireOp",EDGE,"E59.bottom")])]})]});
            var sketch = newSketch(context, id + "F22", { "sketchPlane" : qUnion([Q0])});
            skLineSegment(sketch, "E60.bottom", {"start": v(-15, -10) * mm, "end": v(-65, -10) * mm});
            skLineSegment(sketch, "E60.top", {"start": v(-15, 0.5) * mm, "end": v(-65, 0.5) * mm});
            skLineSegment(sketch, "E60.left", {"start": v(-15, -10) * mm, "end": v(-15, 0.5) * mm});
            skLineSegment(sketch, "E60.right", {"start": v(-65, -10) * mm, "end": v(-65, 0.5) * mm});
            skPoint(sketch, "E60.middle", {"position": v(-40, -4.75) * mm});
            skPoint(sketch, "E60.middle.positionSnap0", {"position": v(-40, -12) * mm});
            skPoint(sketch, "E60.middle.positionSnap1", {"position": v(-67, -4.75) * mm});
            skPoint(sketch, "E60.centerSnap0", {"position": v(-40, -12) * mm});
            skPoint(sketch, "E60.centerSnap1", {"position": v(-67, -4.75) * mm});
            skLineSegment(sketch, "E61.bottom", {"start": v(65, -10) * mm, "end": v(15, -10) * mm});
            skLineSegment(sketch, "E61.top", {"start": v(65, 0.5) * mm, "end": v(15, 0.5) * mm});
            skLineSegment(sketch, "E61.left", {"start": v(65, -10) * mm, "end": v(65, 0.5) * mm});
            skLineSegment(sketch, "E61.right", {"start": v(15, -10) * mm, "end": v(15, 0.5) * mm});
            skPoint(sketch, "E61.middle", {"position": v(40, -4.75) * mm});
            skPoint(sketch, "E61.middle.positionSnap0", {"position": v(40, -12) * mm});
            skPoint(sketch, "E61.middle.positionSnap1", {"position": v(67, -4.75) * mm});
            skPoint(sketch, "E61.centerSnap0", {"position": v(40, -12) * mm});
            skPoint(sketch, "E61.centerSnap1", {"position": v(67, -4.75) * mm});
            skSolve(sketch);
        }
        {
            var Q0;
            Q0=qSketchRegion(id+"F22",true);
            extrude(context, id + "F23", {"entities" : qUnion([Q0]), "operationType" : NewBodyOperationType.REMOVE, "oppositeDirection" : true, "depth" : 37 * mm});
        }
        {
            var Q0;
            Q0=makeQuery(id+"F16.imprint","IMPRINT",FACE,{"disambiguationData":[TD([[makeQuery(id+"F16.imprint","IMPRINT",EDGE,{"derivedFrom":sQuery(id+"F16.wireOp",EDGE,"E54.bottom")}),1.0]])]});
            var sketch = newSketch(context, id + "F24", { "sketchPlane" : qUnion([Q0])});
            skPoint(sketch, "E62.0", {"position": v(-70, 25) * mm});
            skPoint(sketch, "E62.1", {"position": v(-70, -25) * mm});
            skPoint(sketch, "E62.2", {"position": v(70, -25) * mm});
            skPoint(sketch, "E62.3", {"position": v(70, 25) * mm});
            skCircle(sketch, "E63", {"center": v(-70, 25) * mm, "radius": 1.5 * mm});
            skCircle(sketch, "E64", {"center": v(-70, -25) * mm, "radius": 1.5 * mm});
            skCircle(sketch, "E65", {"center": v(70, 25) * mm, "radius": 1.5 * mm});
            skCircle(sketch, "E66", {"center": v(70, -25) * mm, "radius": 1.5 * mm});
            skSolve(sketch);
        }
        {
            var Q0;
            Q0=qSketchRegion(id+"F24",true);
            extrude(context, id + "F25", {"entities" : qUnion([Q0]), "operationType" : NewBodyOperationType.REMOVE, "oppositeDirection" : true, "depth" : 25 * mm});
        }
        {
            var Q0;
            Q0=makeQuery(id+"F9.boolean.opBoolean","COPY",FACE,{"derivedFrom":makeQuery(id+"F9.opExtrude","CAP_FACE",FACE,{"disambiguationData":[OSD([sQuery(id+"F6.wireOp",EDGE,"E22.bottom"),sQuery(id+"F6.wireOp",EDGE,"E22.top"),sQuery(id+"F6.wireOp",EDGE,"E22.left"),sQuery(id+"F6.wireOp",EDGE,"E22.right"),sQuery(id+"F8.wireOp",EDGE,"E25.bottom"),sQuery(id+"F8.wireOp",EDGE,"E25.top"),sQuery(id+"F8.wireOp",EDGE,"E25.left"),sQuery(id+"F8.wireOp",EDGE,"E25.right"),sQuery(id+"F8.wireOp",EDGE,"E27.top"),sQuery(id+"F8.wireOp",EDGE,"E27.left"),sQuery(id+"F8.wireOp",EDGE,"E27.right")])],"isStart":false})});
            var sketch = newSketch(context, id + "F26", { "sketchPlane" : qUnion([Q0])});
            skLineSegment(sketch, "E67.bottom", {"start": v(-48, 37.5) * mm, "end": v(-32, 37.5) * mm});
            skLineSegment(sketch, "E67.top", {"start": v(-48, 34.5) * mm, "end": v(-32, 34.5) * mm});
            skLineSegment(sketch, "E67.left", {"start": v(-48, 37.5) * mm, "end": v(-48, 34.5) * mm});
            skLineSegment(sketch, "E67.right", {"start": v(-32, 37.5) * mm, "end": v(-32, 34.5) * mm});
            skLineSegment(sketch, "E68.bottom", {"start": v(32, 37.5) * mm, "end": v(48, 37.5) * mm});
            skLineSegment(sketch, "E68.top", {"start": v(32, 34.5) * mm, "end": v(48, 34.5) * mm});
            skLineSegment(sketch, "E68.left", {"start": v(32, 37.5) * mm, "end": v(32, 34.5) * mm});
            skLineSegment(sketch, "E68.right", {"start": v(48, 37.5) * mm, "end": v(48, 34.5) * mm});
            skSolve(sketch);
        }
        {
            var Q0;
            Q0=qSketchRegion(id+"F26",true);
            extrude(context, id + "F27", {"entities" : qUnion([Q0]), "operationType" : NewBodyOperationType.REMOVE, "oppositeDirection" : true, "depth" : 3 * mm});
        }
        {
            var Q0;
            Q0=makeQuery(id+"F11.opExtrude","CAP_EDGE",EDGE,{"disambiguationData":[OSD([sQuery(id+"F10.wireOp",EDGE,"E29.right")])],"isStart":false});
            var Q1;
            Q1=makeQuery(id+"F11.opExtrude","CAP_EDGE",EDGE,{"disambiguationData":[OSD([sQuery(id+"F10.wireOp",EDGE,"E29.top")])],"isStart":false});
            var Q2;
            Q2=makeQuery(id+"F11.opExtrude","CAP_EDGE",EDGE,{"disambiguationData":[OSD([sQuery(id+"F10.wireOp",EDGE,"E29.left")])],"isStart":false});
            var Q3;
            Q3=makeQuery(id+"F11.opExtrude","CAP_EDGE",EDGE,{"disambiguationData":[OSD([sQuery(id+"F10.wireOp",EDGE,"E29.bottom")])],"isStart":false});
            fillet(context, id + "F28", {"entities" : qUnion([Q0, Q1, Q2, Q3]), "radius" : 0.5 * mm, "tangentPropagation" : true, "allowEdgeOverflow" : false});
        }
        {
            var Q0;
            Q0=makeQuery(id+"F21.opExtrude","SWEPT_FACE",FACE,{"disambiguationData":[OSD([sQuery(id+"F20.wireOp",EDGE,"E58.left")])]});
            var sketch = newSketch(context, id + "F29", { "sketchPlane" : qUnion([Q0])});
            skLineSegment(sketch, "E69.bottom", {"start": v(34.5, -5) * mm, "end": v(14.5, -5) * mm});
            skLineSegment(sketch, "E69.top", {"start": v(34.5, -10) * mm, "end": v(14.5, -10) * mm});
            skLineSegment(sketch, "E69.left", {"start": v(34.5, -5) * mm, "end": v(34.5, -10) * mm});
            skLineSegment(sketch, "E69.right", {"start": v(14.5, -5) * mm, "end": v(14.5, -10) * mm});
            skSolve(sketch);
        }
        {
            var Q0;
            Q0=makeQuery(id+"F21.boolean.opBoolean","MERGE",FACE,{"derivedFrom":[makeQuery(id+"F5.boolean.opBoolean","COPY",FACE,{"derivedFrom":makeQuery(id+"F5.opExtrude","SWEPT_FACE",FACE,{"disambiguationData":[OSD([sQuery(id+"F4.wireOp",EDGE,"E19.right")])]})}),makeQuery(id+"F21.opExtrude","SWEPT_FACE",FACE,{"disambiguationData":[OSD([sQuery(id+"F20.wireOp",EDGE,"E59.left")])]})]});
            var sketch = newSketch(context, id + "F30", { "sketchPlane" : qUnion([Q0])});
            skLineSegment(sketch, "E70.bottom", {"start": v(34.5, -5) * mm, "end": v(14.5, -5) * mm});
            skLineSegment(sketch, "E70.top", {"start": v(34.5, -10) * mm, "end": v(14.5, -10) * mm});
            skLineSegment(sketch, "E70.left", {"start": v(34.5, -5) * mm, "end": v(34.5, -10) * mm});
            skLineSegment(sketch, "E70.right", {"start": v(14.5, -5) * mm, "end": v(14.5, -10) * mm});
            skSolve(sketch);
        }
        {
            var Q0;
            Q0=makeQuery(id+"F30.imprint","IMPRINT",FACE,{"disambiguationData":[TD([[makeQuery(id+"F30.imprint","IMPRINT",EDGE,{"derivedFrom":sQuery(id+"F30.wireOp",EDGE,"E70.bottom")}),1.0]])]});
            var Q1;
            Q1=makeQuery(id+"F29.imprint","IMPRINT",FACE,{"disambiguationData":[TD([[makeQuery(id+"F29.imprint","IMPRINT",EDGE,{"derivedFrom":sQuery(id+"F29.wireOp",EDGE,"E69.bottom")}),1.0]])]});
            extrude(context, id + "F31", {"entities" : qUnion([Q0, Q1]), "operationType" : NewBodyOperationType.REMOVE, "oppositeDirection" : true, "depth" : 4 * mm});
        }
        {
            var Q0;
            Q0=makeQuery(id+"F31.boolean.opBoolean","COPY",FACE,{"derivedFrom":makeQuery(id+"F31.opExtrude","SWEPT_FACE",FACE,{"disambiguationData":[OSD([sQuery(id+"F29.wireOp",EDGE,"E69.bottom")])]})});
            var sketch = newSketch(context, id + "F32", { "sketchPlane" : qUnion([Q0])});
            skLineSegment(sketch, "E71.bottom", {"start": v(-15, -34.5) * mm, "end": v(-13, -34.5) * mm});
            skLineSegment(sketch, "E71.top", {"start": v(-15, -14.5) * mm, "end": v(-13, -14.5) * mm});
            skLineSegment(sketch, "E71.left", {"start": v(-15, -34.5) * mm, "end": v(-15, -14.5) * mm});
            skLineSegment(sketch, "E71.right", {"start": v(-13, -34.5) * mm, "end": v(-13, -14.5) * mm});
            skSolve(sketch);
        }
        {
            var Q0;
            Q0=qSketchRegion(id+"F32",true);
            extrude(context, id + "F33", {"entities" : qUnion([Q0]), "operationType" : NewBodyOperationType.REMOVE, "oppositeDirection" : true, "depth" : 0.5 * mm});
        }
    });
